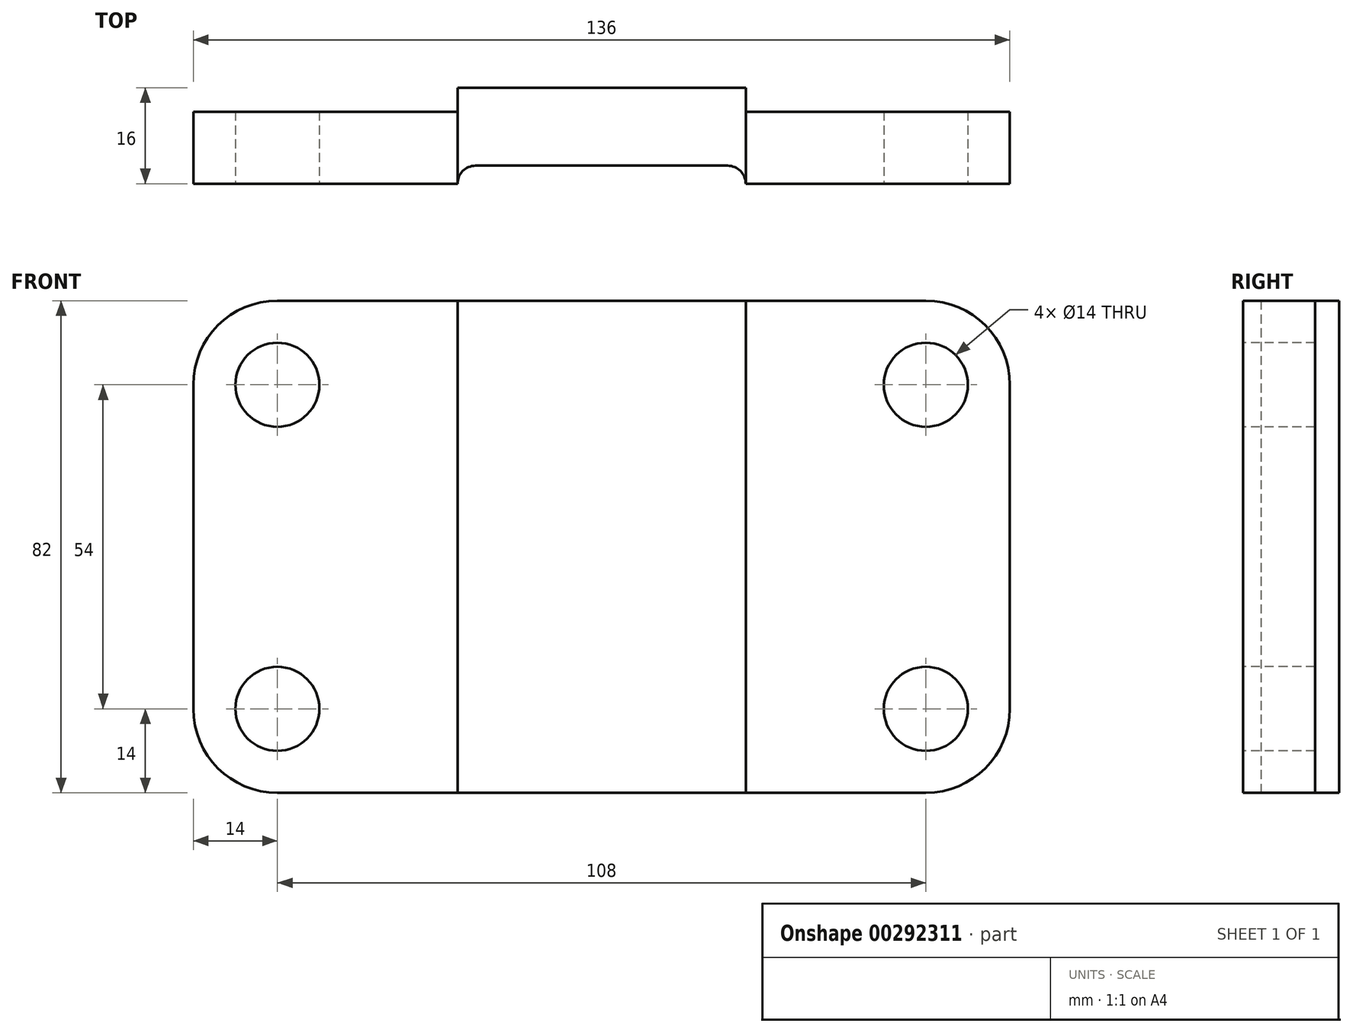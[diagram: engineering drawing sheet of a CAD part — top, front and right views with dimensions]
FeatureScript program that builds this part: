
annotation { "Feature Type Name" : "Feature", "Feature Type Description" : "" }
export const myFeature = defineFeature(function(context is Context, id is Id, definition is map)
    precondition{}
    {
        {
            var Q0;
            Q0=qCreatedBy(makeId("Front.planeOp"),FACE);
            var sketch = newSketch(context, id + "F0", { "sketchPlane" : qUnion([Q0])});
            skArc(sketch, "E0", {"start": v(-14, 0) * mm, "mid": v(-9.9, -9.9) * mm, "end": v(0, -14) * mm});
            skArc(sketch, "E1", {"start": v(108, -14) * mm, "mid": v(117.9, -9.9) * mm, "end": v(122, 0) * mm});
            skArc(sketch, "E2", {"start": v(0, 68) * mm, "mid": v(-9.9, 63.9) * mm, "end": v(-14, 54) * mm});
            skArc(sketch, "E3", {"start": v(122, 54) * mm, "mid": v(117.9, 63.9) * mm, "end": v(108, 68) * mm});
            skLineSegment(sketch, "E4", {"start": v(0, 68) * mm, "end": v(108, 68) * mm});
            skLineSegment(sketch, "E5", {"start": v(-14, 54) * mm, "end": v(-14, 0) * mm});
            skLineSegment(sketch, "E6", {"start": v(0, -14) * mm, "end": v(108, -14) * mm});
            skLineSegment(sketch, "E7", {"start": v(122, 0) * mm, "end": v(122, 54) * mm});
            skLineSegment(sketch, "E8", {"start": v(30, -14) * mm, "end": v(30, 68) * mm});
            skLineSegment(sketch, "E9", {"start": v(78, 68) * mm, "end": v(78, -14) * mm});
            skSolve(sketch);
        }
        {
            var Q0;
            {var subQ3=sQuery(id+"F0.wireOp",EDGE,"E0");Q0=makeQuery(id+"F0.imprint","IMPRINT",FACE,{"disambiguationData":[TD([[makeQuery(id+"F0.imprint","IMPRINT",EDGE,{"derivedFrom":subQ3}),1.0]])]});}
            var Q1;
            {var subQ1=sQuery(id+"F0.wireOp",EDGE,"E1");Q1=makeQuery(id+"F0.imprint","IMPRINT",FACE,{"disambiguationData":[TD([[makeQuery(id+"F0.imprint","IMPRINT",EDGE,{"derivedFrom":subQ1}),1.0]])]});}
            extrude(context, id + "F1", {"entities" : qUnion([Q0, Q1]), "depth" : 12 * mm});
        }
        {
            var Q0;
            {var subQ0=sQuery(id+"F0.wireOp",EDGE,"E8");Q0=makeQuery(id+"F0.imprint","IMPRINT",FACE,{"disambiguationData":[TD([[makeQuery(id+"F0.imprint","IMPRINT",EDGE,{"derivedFrom":subQ0}),-1.0]])]});}
            extrude(context, id + "F2", {"entities" : qUnion([Q0]), "depth" : 12 * mm, "hasSecondDirection" : true, "secondDirectionOppositeDirection" : true, "secondDirectionDepth" : 4 * mm});
        }
        {
            var Q0;
            Q0=makeQuery(id+"F1.opExtrude","CAP_FACE",FACE,{"disambiguationData":[OSD([sQuery(id+"F0.wireOp",EDGE,"E0"),sQuery(id+"F0.wireOp",EDGE,"E2"),sQuery(id+"F0.wireOp",EDGE,"E4"),sQuery(id+"F0.wireOp",EDGE,"E5"),sQuery(id+"F0.wireOp",EDGE,"E6"),sQuery(id+"F0.wireOp",EDGE,"E8")])],"isStart":false});
            var sketch = newSketch(context, id + "F3", { "sketchPlane" : qUnion([Q0])});
            skCircle(sketch, "E10", {"center": v(0, 0) * mm, "radius": 7 * mm});
            skCircle(sketch, "E11.0.1.0", {"center": v(0, 54) * mm, "radius": 7 * mm});
            skCircle(sketch, "E11.1.0.0", {"center": v(108, 0) * mm, "radius": 7 * mm});
            skCircle(sketch, "E11.1.1.0", {"center": v(108, 54) * mm, "radius": 7 * mm});
            skLineSegment(sketch, "E11.direction1", {"start": v(0, 0) * mm, "end": v(108, 0) * mm, "construction": true});
            skLineSegment(sketch, "E11.direction2", {"start": v(0, 0) * mm, "end": v(0, 54) * mm, "construction": true});
            skSolve(sketch);
        }
        {
            var Q0;
            Q0=makeQuery(id+"F3.imprint","IMPRINT",FACE,{"disambiguationData":[TD([[makeQuery(id+"F3.imprint","IMPRINT",EDGE,{"derivedFrom":sQuery(id+"F3.wireOp",EDGE,"E10")}),1.0]])]});
            var Q1;
            Q1=makeQuery(id+"F3.imprint","IMPRINT",FACE,{"disambiguationData":[TD([[makeQuery(id+"F3.imprint","IMPRINT",EDGE,{"derivedFrom":sQuery(id+"F3.wireOp",EDGE,"E11.0.1.0")}),1.0]])]});
            var Q2;
            Q2=makeQuery(id+"F3.imprint","IMPRINT",FACE,{"disambiguationData":[TD([[makeQuery(id+"F3.imprint","IMPRINT",EDGE,{"derivedFrom":sQuery(id+"F3.wireOp",EDGE,"E11.1.1.0")}),1.0]])]});
            var Q3;
            Q3=makeQuery(id+"F3.imprint","IMPRINT",FACE,{"disambiguationData":[TD([[makeQuery(id+"F3.imprint","IMPRINT",EDGE,{"derivedFrom":sQuery(id+"F3.wireOp",EDGE,"E11.1.0.0")}),1.0]])]});
            extrude(context, id + "F4", {"entities" : qUnion([Q0, Q1, Q2, Q3]), "operationType" : NewBodyOperationType.REMOVE, "endBound" : BoundingType.THROUGH_ALL, "oppositeDirection" : true, "depth" : 25 * mm});
        }
        {
            var Q0;
            Q0=makeQuery(id+"F3.imprint","IMPRINT",FACE,{"disambiguationData":[TD([[makeQuery(id+"F3.imprint","IMPRINT",EDGE,{"derivedFrom":sQuery(id+"F3.wireOp",EDGE,"E11.1.1.0")}),1.0]])]});
            var Q1;
            Q1=makeQuery(id+"F3.imprint","IMPRINT",FACE,{"disambiguationData":[TD([[makeQuery(id+"F3.imprint","IMPRINT",EDGE,{"derivedFrom":sQuery(id+"F3.wireOp",EDGE,"E11.1.0.0")}),1.0]])]});
            extrude(context, id + "F5", {"entities" : qUnion([Q0, Q1]), "operationType" : NewBodyOperationType.REMOVE, "oppositeDirection" : true, "depth" : 25 * mm});
        }
        {
            var Q0;
            Q0=makeQuery(id+"F2.opExtrude","SWEPT_FACE",FACE,{"disambiguationData":[OSD([sQuery(id+"F0.wireOp",EDGE,"E6")])]});
            var sketch = newSketch(context, id + "F6", { "sketchPlane" : qUnion([Q0])});
            skArc(sketch, "E12", {"start": v(30, 12) * mm, "mid": v(30.88, 9.88) * mm, "end": v(33, 9) * mm});
            skArc(sketch, "E13", {"start": v(75, 9) * mm, "mid": v(77.12, 9.88) * mm, "end": v(78, 12) * mm});
            skLineSegment(sketch, "E14", {"start": v(33, 9) * mm, "end": v(75, 9) * mm});
            skLineSegment(sketch, "E15", {"start": v(30, 12) * mm, "end": v(78, 12) * mm});
            skSolve(sketch);
        }
        {
            var Q0;
            Q0 = qSketchRegion(id + "F6", true);
            extrude(context, id + "F7", {"entities" : qUnion([Q0]), "operationType" : NewBodyOperationType.REMOVE, "endBound" : BoundingType.THROUGH_ALL, "oppositeDirection" : true, "depth" : 25 * mm});
        }
    });
